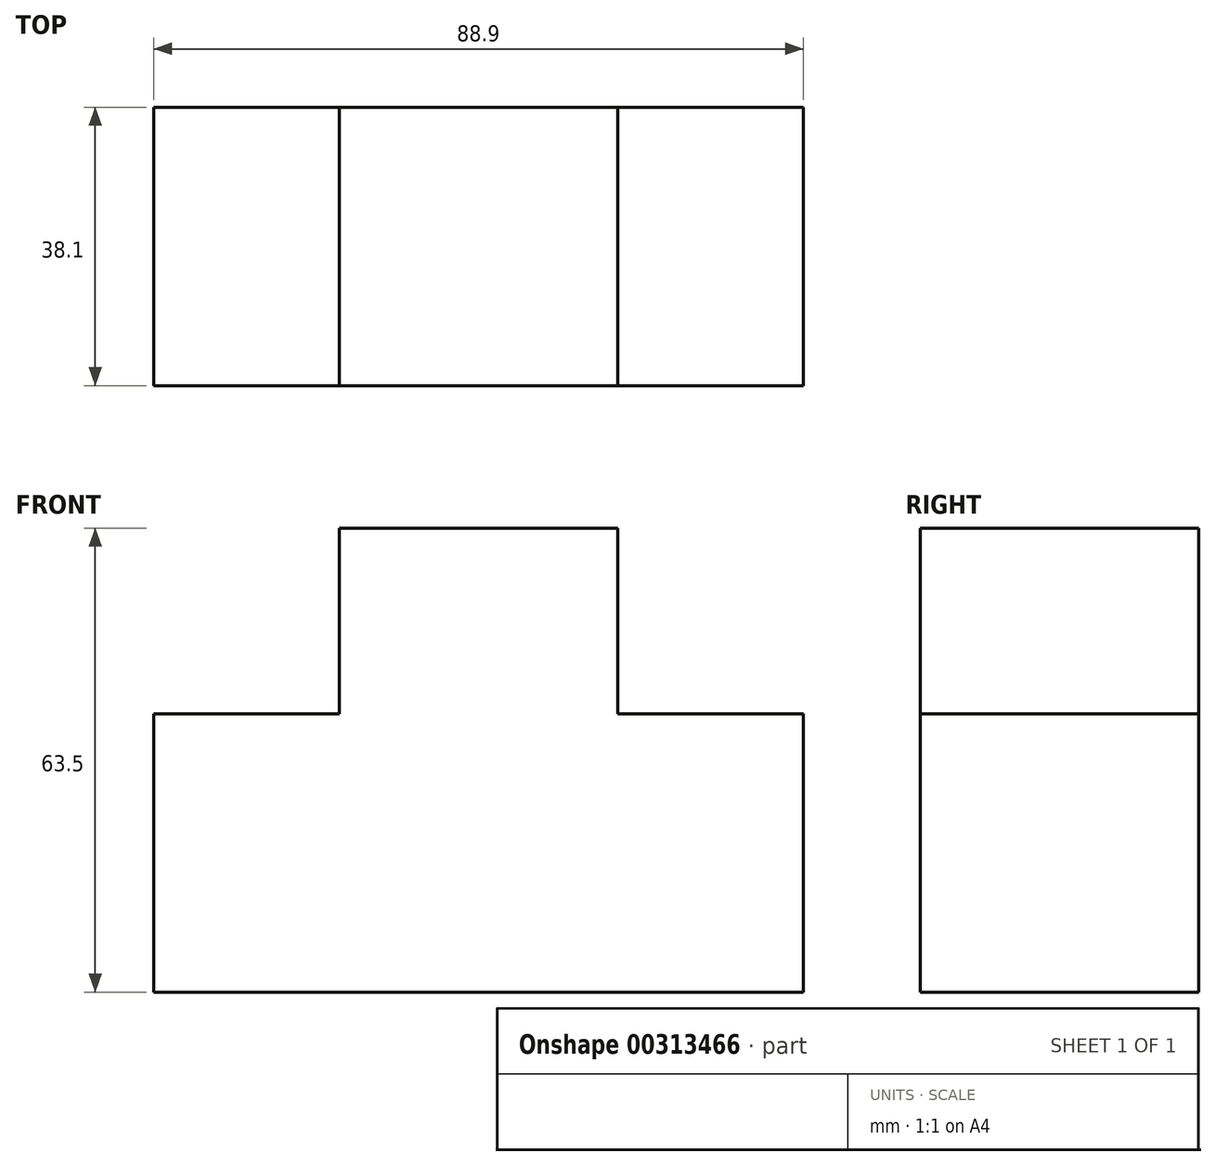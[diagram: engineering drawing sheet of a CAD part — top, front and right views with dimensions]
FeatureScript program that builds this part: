
annotation { "Feature Type Name" : "Feature", "Feature Type Description" : "" }
export const myFeature = defineFeature(function(context is Context, id is Id, definition is map)
    precondition{}
    {
        {
            var Q0;
            Q0=qCreatedBy(makeId("Front.planeOp"),FACE);
            var sketch = newSketch(context, id + "F0", { "sketchPlane" : qUnion([Q0])});
            skLineSegment(sketch, "E0", {"start": v(-41.5, -31.18) * mm, "end": v(47.4, -31.18) * mm});
            skLineSegment(sketch, "E1", {"start": v(47.4, -31.18) * mm, "end": v(47.4, 6.92) * mm});
            skLineSegment(sketch, "E2", {"start": v(47.4, 6.92) * mm, "end": v(22, 6.92) * mm});
            skLineSegment(sketch, "E3", {"start": v(22, 6.92) * mm, "end": v(22, 32.32) * mm});
            skLineSegment(sketch, "E4", {"start": v(22, 32.32) * mm, "end": v(-16.1, 32.32) * mm});
            skLineSegment(sketch, "E5", {"start": v(-16.1, 32.32) * mm, "end": v(-16.1, 6.92) * mm});
            skLineSegment(sketch, "E6", {"start": v(-16.1, 6.92) * mm, "end": v(-41.5, 6.92) * mm});
            skLineSegment(sketch, "E7", {"start": v(-41.5, 6.92) * mm, "end": v(-41.5, -31.18) * mm});
            skSolve(sketch);
        }
        {
            var Q0;
            Q0=makeQuery(id+"F0.imprint","IMPRINT",FACE,{"disambiguationData":[TD([[makeQuery(id+"F0.imprint","IMPRINT",EDGE,{"derivedFrom":sQuery(id+"F0.wireOp",EDGE,"E0")}),1.0]])]});
            extrude(context, id + "F1", {"entities" : qUnion([Q0]), "depth" : 38.1 * mm});
        }
    });
